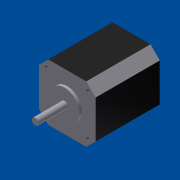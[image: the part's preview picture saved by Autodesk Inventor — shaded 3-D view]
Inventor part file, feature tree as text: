
AUTODESK INVENTOR PART (.ipt)
format: ipt  version: 2012 SP1 (Build 160190100, 190)  size: 121,856 bytes
history: native  units: in
note: dims shown in document units (in); Inventor stores cm internally (conversion verified against a paired STEP export)
features: sketch x5, extrude x4, hole x1, pattern_linear x1, chamfer x1
ambient origin geometry x8: Origin, YZ Plane, XZ Plane, XY Plane, X Axis, Y Axis, Z Axis, Center Point
bodies: Solid1 (feature_tree)
feature tree (12):
  extrude  "Extrusion1"  Depth=1.67in
  hole  "Hole1"  [1 undecoded]
  pattern_linear  "Rectangular Pattern1"  Count1=2 Spacing1=1.22in
  extrude  "Extrusion2"  Depth=0.7874in
  extrude  "Extrusion3"  Depth=0.87in
  chamfer  "Chamfer1"  Distance=0.0787in
  extrude  "Extrusion4"  Depth=0.1969in
  sketch  "Sketch1"  dims[d0=1.67in d1=1.67in]
  sketch  "Sketch2"  dims[d2=1.89in d3=0.0in d4=0.1181in]
  sketch  "Sketch3"  dims[d5=0.225in]
  sketch  "Sketch4"  dims[d6=0.225in]
  sketch  "Sketch5"  dims[d7=0.097in d8=0.1575in d9=0.375in d10=0.25in d11=0.5635in d12=0.1772in d13=0.8108in d14=0.7874in d16=1.22in d17=0.7874in d19=1.22in d20=0.87in d21=0.0787in d22=0.0in d23=0.1969in d24=0.8661in d25=0.0in d26=0.2756in d27=0.125in d28=45.0deg d29=0.1969in d30=0.835in d31=0.835in d32=0.3937in d33=0.0in]
note: 1 required parameter value undecoded (feature->parameter linkage not recoverable at this tier; creation-order binding heuristic only, values carry confidence <= 0.55)
